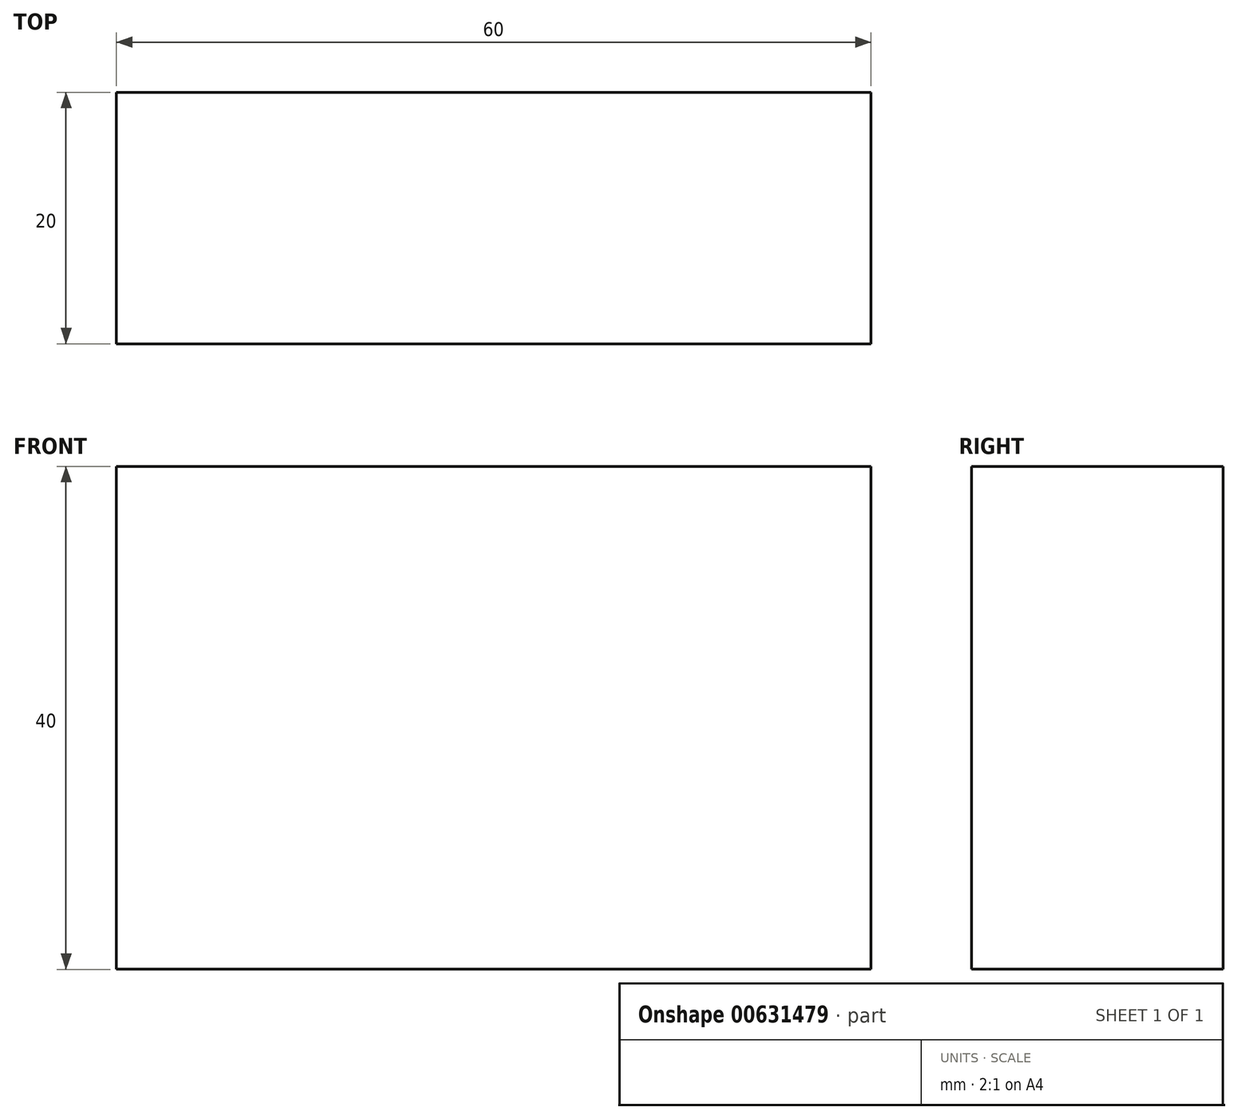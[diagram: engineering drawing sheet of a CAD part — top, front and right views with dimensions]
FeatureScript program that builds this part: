
annotation { "Feature Type Name" : "Feature", "Feature Type Description" : "" }
export const myFeature = defineFeature(function(context is Context, id is Id, definition is map)
    precondition{}
    {
        {
            var Q0;
            Q0=qCreatedBy(makeId("Front.planeOp"),FACE);
            var sketch = newSketch(context, id + "F0", { "sketchPlane" : qUnion([Q0])});
            skLineSegment(sketch, "E0", {"start": v(-28.17, 44.01) * mm, "end": v(31.83, 44.01) * mm});
            skLineSegment(sketch, "E1", {"start": v(31.83, 44.01) * mm, "end": v(31.83, 4.01) * mm});
            skLineSegment(sketch, "E2", {"start": v(31.83, 4.01) * mm, "end": v(-28.17, 4.01) * mm});
            skLineSegment(sketch, "E3", {"start": v(-28.17, 4.01) * mm, "end": v(-28.17, 44.01) * mm});
            skSolve(sketch);
        }
        {
            var Q0;
            Q0=makeQuery(id+"F0.imprint","IMPRINT",FACE,{"disambiguationData":[TD([[makeQuery(id+"F0.imprint","IMPRINT",EDGE,{"derivedFrom":sQuery(id+"F0.wireOp",EDGE,"E0")}),-1.0]])]});
            extrude(context, id + "F1", {"entities" : qUnion([Q0]), "depth" : 20 * mm, "offsetDistance" : 25 * mm});
        }
    });
